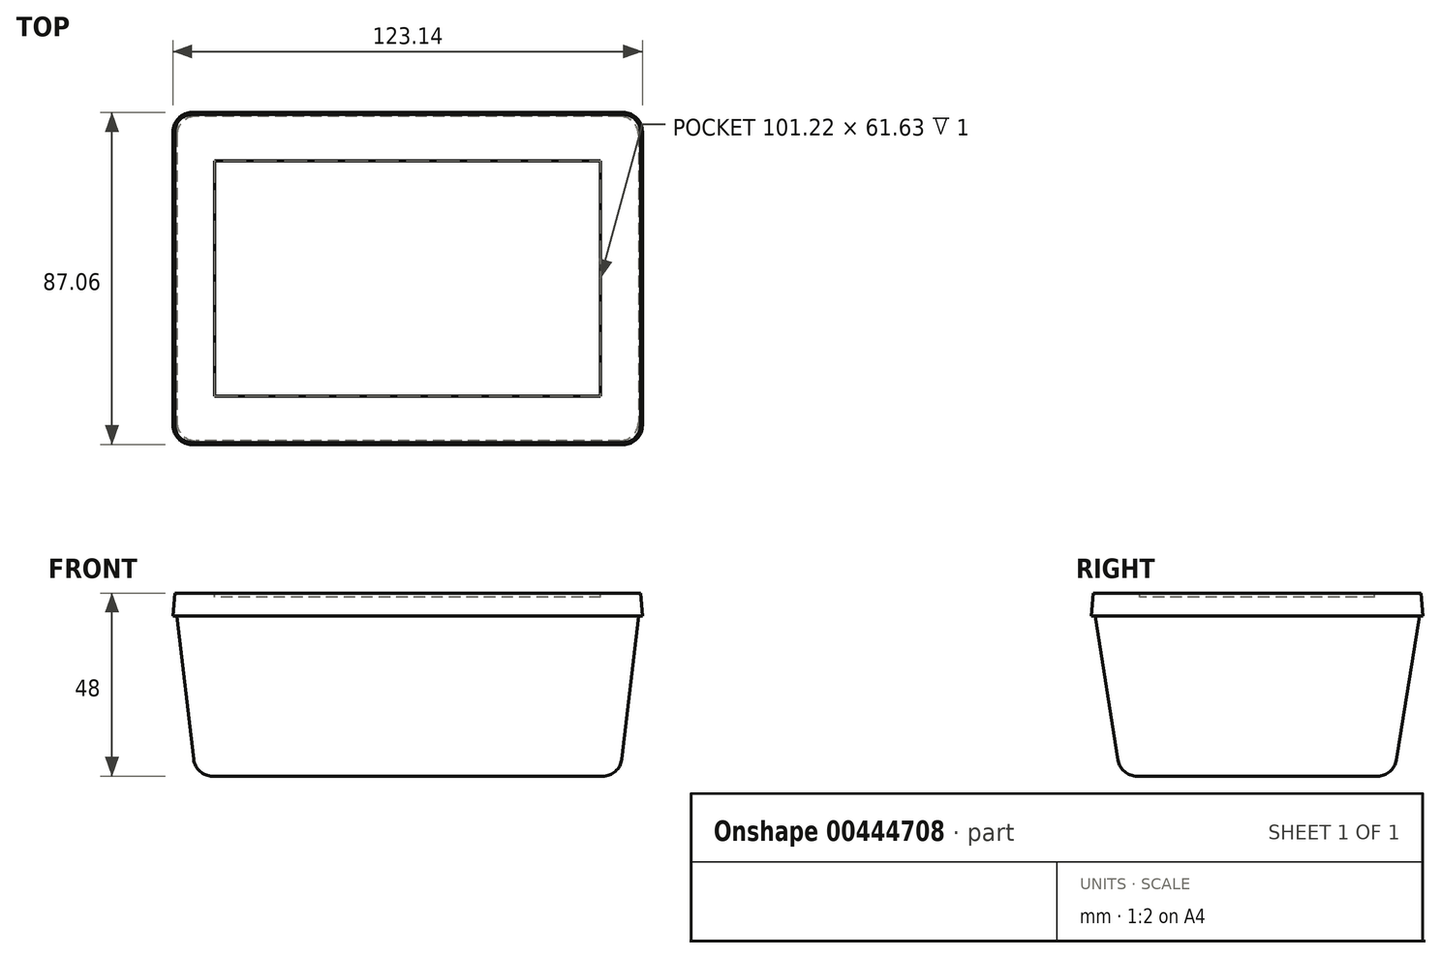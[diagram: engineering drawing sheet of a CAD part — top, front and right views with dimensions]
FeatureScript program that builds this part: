
annotation { "Feature Type Name" : "Feature", "Feature Type Description" : "" }
export const myFeature = defineFeature(function(context is Context, id is Id, definition is map)
    precondition{}
    {
        {
            var Q0;
            Q0=qCreatedBy(makeId("Top.planeOp"),FACE);
            var sketch = newSketch(context, id + "F0", { "sketchPlane" : qUnion([Q0])});
            skLineSegment(sketch, "E0.bottom", {"start": v(55.6, 35.81) * mm, "end": v(-55.6, 35.81) * mm});
            skLineSegment(sketch, "E0.top", {"start": v(55.6, -35.81) * mm, "end": v(-55.6, -35.81) * mm});
            skLineSegment(sketch, "E0.left", {"start": v(55.6, 35.81) * mm, "end": v(55.6, -35.81) * mm});
            skLineSegment(sketch, "E0.right", {"start": v(-55.6, 35.81) * mm, "end": v(-55.6, -35.81) * mm});
            skPoint(sketch, "E0.middle", {"position": v(0, 0) * mm});
            skSolve(sketch);
        }
        {
            var Q0;
            Q0=makeQuery(id+"F0.imprint","IMPRINT",FACE,{"disambiguationData":[TD([[makeQuery(id+"F0.imprint","IMPRINT",EDGE,{"derivedFrom":sQuery(id+"F0.wireOp",EDGE,"E0.bottom")}),1.0]])]});
            cPlane(context, id + "F1", {"entities" : qUnion([Q0]), "cplaneType" : CPlaneType.OFFSET, "offset" : 42 * mm, "width" : 150 * mm, "height" : 150 * mm});
        }
        {
            var Q0;
            Q0=qCreatedBy(id+"F1.planeOp",FACE);
            var sketch = newSketch(context, id + "F2", { "sketchPlane" : qUnion([Q0])});
            skLineSegment(sketch, "E1.bottom", {"start": v(60.57, 42.53) * mm, "end": v(-60.57, 42.53) * mm});
            skLineSegment(sketch, "E1.top", {"start": v(60.57, -42.53) * mm, "end": v(-60.57, -42.53) * mm});
            skLineSegment(sketch, "E1.left", {"start": v(60.57, 42.53) * mm, "end": v(60.57, -42.53) * mm});
            skLineSegment(sketch, "E1.right", {"start": v(-60.57, 42.53) * mm, "end": v(-60.57, -42.53) * mm});
            skPoint(sketch, "E1.middle", {"position": v(0, 0) * mm});
            skSolve(sketch);
        }
        {
            var Q0;
            Q0=makeQuery(id+"F0.imprint","IMPRINT",FACE,{"disambiguationData":[TD([[makeQuery(id+"F0.imprint","IMPRINT",EDGE,{"derivedFrom":sQuery(id+"F0.wireOp",EDGE,"E0.bottom")}),1.0]])]});
            var Q1;
            Q1=makeQuery(id+"F2.imprint","IMPRINT",FACE,{"disambiguationData":[TD([[makeQuery(id+"F2.imprint","IMPRINT",EDGE,{"derivedFrom":sQuery(id+"F2.wireOp",EDGE,"E1.bottom")}),1.0]])]});
            loft(context, id + "F3", {"sheetProfilesArray" : [{ "sheetProfileEntities" : qUnion([Q0]) }, { "sheetProfileEntities" : qUnion([Q1]) }]});
        }
        {
            var Q0;
            Q0=makeQuery(id+"F3.opLoft","MID_CAP_EDGE",EDGE,{"disambiguationData":[OSD([sQuery(id+"F0.wireOp",EDGE,"E0.bottom"),sQuery(id+"F0.wireOp",EDGE,"E0.top"),sQuery(id+"F0.wireOp",EDGE,"E0.right")])],"capPos":0.0});
            var Q1;
            Q1=makeQuery(id+"F3.opLoft","SWEPT_EDGE",EDGE,{"disambiguationData":[OSD([sQuery(id+"F0.wireOp",EDGE,"E0.bottom"),sQuery(id+"F0.wireOp",EDGE,"E0.right"),sQuery(id+"F2.wireOp",EDGE,"E1.bottom"),sQuery(id+"F2.wireOp",EDGE,"E1.right")])]});
            var Q2;
            Q2=makeQuery(id+"F3.opLoft","MID_CAP_EDGE",EDGE,{"disambiguationData":[OSD([sQuery(id+"F0.wireOp",EDGE,"E0.bottom"),sQuery(id+"F0.wireOp",EDGE,"E0.left"),sQuery(id+"F0.wireOp",EDGE,"E0.right")])],"capPos":0.0});
            var Q3;
            Q3=makeQuery(id+"F3.opLoft","MID_CAP_EDGE",EDGE,{"disambiguationData":[OSD([sQuery(id+"F0.wireOp",EDGE,"E0.bottom"),sQuery(id+"F0.wireOp",EDGE,"E0.top"),sQuery(id+"F0.wireOp",EDGE,"E0.left")])],"capPos":0.0});
            var Q4;
            Q4=makeQuery(id+"F3.opLoft","SWEPT_EDGE",EDGE,{"disambiguationData":[OSD([sQuery(id+"F0.wireOp",EDGE,"E0.bottom"),sQuery(id+"F0.wireOp",EDGE,"E0.left"),sQuery(id+"F2.wireOp",EDGE,"E1.bottom"),sQuery(id+"F2.wireOp",EDGE,"E1.left")])]});
            var Q5;
            Q5=makeQuery(id+"F3.opLoft","SWEPT_EDGE",EDGE,{"disambiguationData":[OSD([sQuery(id+"F0.wireOp",EDGE,"E0.top"),sQuery(id+"F0.wireOp",EDGE,"E0.right"),sQuery(id+"F2.wireOp",EDGE,"E1.top"),sQuery(id+"F2.wireOp",EDGE,"E1.right")])]});
            var Q6;
            Q6=makeQuery(id+"F3.opLoft","MID_CAP_EDGE",EDGE,{"disambiguationData":[OSD([sQuery(id+"F0.wireOp",EDGE,"E0.top"),sQuery(id+"F0.wireOp",EDGE,"E0.left"),sQuery(id+"F0.wireOp",EDGE,"E0.right")])],"capPos":0.0});
            var Q7;
            Q7=makeQuery(id+"F3.opLoft","SWEPT_EDGE",EDGE,{"disambiguationData":[OSD([sQuery(id+"F0.wireOp",EDGE,"E0.top"),sQuery(id+"F0.wireOp",EDGE,"E0.left"),sQuery(id+"F2.wireOp",EDGE,"E1.top"),sQuery(id+"F2.wireOp",EDGE,"E1.left")])]});
            fillet(context, id + "F4", {"entities" : qUnion([Q0, Q1, Q2, Q3, Q4, Q5, Q6, Q7]), "radius" : 5 * mm, "tangentPropagation" : true, "allowEdgeOverflow" : false});
        }
        {
            var Q0;
            Q0=makeQuery(id+"F3.opLoft","CAP_FACE",FACE,{"disambiguationData":[OSD([makeQuery(id+"F2.imprint","IMPRINT",FACE,{"disambiguationData":[TD([[makeQuery(id+"F2.imprint","IMPRINT",EDGE,{"derivedFrom":sQuery(id+"F2.wireOp",EDGE,"E1.bottom")}),1.0]])]})])],"isStart":true});
            var sketch = newSketch(context, id + "F5", { "sketchPlane" : qUnion([Q0])});
            skLineSegment(sketch, "E2.bottom", {"start": v(61.57, 43.53) * mm, "end": v(-61.57, 43.53) * mm});
            skLineSegment(sketch, "E2.top", {"start": v(61.57, -43.53) * mm, "end": v(-61.57, -43.53) * mm});
            skLineSegment(sketch, "E2.left", {"start": v(61.57, 43.53) * mm, "end": v(61.57, -43.53) * mm});
            skLineSegment(sketch, "E2.right", {"start": v(-61.57, 43.53) * mm, "end": v(-61.57, -43.53) * mm});
            skPoint(sketch, "E2.middle", {"position": v(0, 0) * mm});
            skSolve(sketch);
        }
        {
            var Q0;
            Q0=makeQuery(id+"F5.imprint","IMPRINT",FACE,{"disambiguationData":[TD([[makeQuery(id+"F5.imprint","IMPRINT",EDGE,{"derivedFrom":sQuery(id+"F5.wireOp",EDGE,"E2.bottom")}),1.0]])]});
            var Q1;
            {var subQ0=sQuery(id+"F2.wireOp",EDGE,"E1.bottom");var subQ2=sQuery(id+"F2.wireOp",EDGE,"E1.left");var subQ3=sQuery(id+"F2.wireOp",EDGE,"E1.right");Q1=makeQuery(id+"F5.imprint","IMPRINT",FACE,{"disambiguationData":[TD([[makeQuery(id+"F5.imprint","IMPRINT",EDGE,{"derivedFrom":makeQuery(id+"F3.opLoft","MID_CAP_EDGE",EDGE,{"disambiguationData":[OSD([subQ0,subQ2,subQ3])],"capPos":1.0})}),1.0]])]});}
            extrude(context, id + "F6", {"entities" : qUnion([Q0, Q1]), "operationType" : NewBodyOperationType.ADD, "depth" : 6 * mm});
        }
        {
            var Q0;
            Q0=makeQuery(id+"F6.opExtrude","CAP_FACE",FACE,{"disambiguationData":[OSD([sQuery(id+"F5.wireOp",EDGE,"E2.bottom"),sQuery(id+"F5.wireOp",EDGE,"E2.top"),sQuery(id+"F5.wireOp",EDGE,"E2.left"),sQuery(id+"F5.wireOp",EDGE,"E2.right")])],"isStart":false});
            var sketch = newSketch(context, id + "F7", { "sketchPlane" : qUnion([Q0])});
            skLineSegment(sketch, "E3.bottom", {"start": v(50.6, 30.82) * mm, "end": v(-50.6, 30.82) * mm});
            skLineSegment(sketch, "E3.top", {"start": v(50.6, -30.82) * mm, "end": v(-50.6, -30.82) * mm});
            skLineSegment(sketch, "E3.left", {"start": v(50.6, 30.82) * mm, "end": v(50.6, -30.82) * mm});
            skLineSegment(sketch, "E3.right", {"start": v(-50.6, 30.82) * mm, "end": v(-50.6, -30.81) * mm});
            skPoint(sketch, "E3.middle", {"position": v(0, 0) * mm});
            skSolve(sketch);
        }
        {
            var Q0;
            Q0 = qSketchRegion(id + "F7", true);
            extrude(context, id + "F8", {"entities" : qUnion([Q0]), "operationType" : NewBodyOperationType.REMOVE, "oppositeDirection" : true, "depth" : 1 * mm});
        }
        {
            var Q0;
            Q0=makeQuery(id+"F6.opExtrude","SWEPT_EDGE",EDGE,{"disambiguationData":[OSD([sQuery(id+"F5.wireOp",EDGE,"E2.bottom"),sQuery(id+"F5.wireOp",EDGE,"E2.right")])]});
            var Q1;
            Q1=makeQuery(id+"F6.opExtrude","SWEPT_EDGE",EDGE,{"disambiguationData":[OSD([sQuery(id+"F5.wireOp",EDGE,"E2.top"),sQuery(id+"F5.wireOp",EDGE,"E2.right")])]});
            var Q2;
            Q2=makeQuery(id+"F6.opExtrude","SWEPT_EDGE",EDGE,{"disambiguationData":[OSD([sQuery(id+"F5.wireOp",EDGE,"E2.top"),sQuery(id+"F5.wireOp",EDGE,"E2.left")])]});
            var Q3;
            Q3=makeQuery(id+"F6.opExtrude","SWEPT_EDGE",EDGE,{"disambiguationData":[OSD([sQuery(id+"F5.wireOp",EDGE,"E2.bottom"),sQuery(id+"F5.wireOp",EDGE,"E2.left")])]});
            fillet(context, id + "F9", {"entities" : qUnion([Q0, Q1, Q2, Q3]), "radius" : 5 * mm, "tangentPropagation" : true, "allowEdgeOverflow" : false});
        }
        {
            var Q0;
            Q0=makeQuery(id+"F6.opExtrude","CAP_EDGE",EDGE,{"disambiguationData":[OSD([sQuery(id+"F5.wireOp",EDGE,"E2.left")])],"isStart":false});
            var Q1;
            {var subQ0=sQuery(id+"F5.wireOp",EDGE,"E2.left");var subQ1=sQuery(id+"F5.wireOp",EDGE,"E2.bottom");Q1=makeQuery(id+"F9.opFillet","BLEND_EDGE",EDGE,{"blendedFrom":[makeQuery(id+"F6.opExtrude","SWEPT_EDGE",EDGE,{"disambiguationData":[OSD([subQ1,subQ0])]}),makeQuery(id+"F6.opExtrude","CAP_FACE",FACE,{"disambiguationData":[OSD([subQ1,sQuery(id+"F5.wireOp",EDGE,"E2.top"),subQ0,sQuery(id+"F5.wireOp",EDGE,"E2.right")])],"isStart":false})],"blendedInto":[makeQuery(id+"F6.opExtrude","CAP_FACE",FACE,{"disambiguationData":[OSD([subQ1,sQuery(id+"F5.wireOp",EDGE,"E2.top"),subQ0,sQuery(id+"F5.wireOp",EDGE,"E2.right")])],"isStart":false})]});}
            var Q2;
            Q2=makeQuery(id+"F6.opExtrude","CAP_EDGE",EDGE,{"disambiguationData":[OSD([sQuery(id+"F5.wireOp",EDGE,"E2.bottom")])],"isStart":false});
            var Q3;
            {var subQ0=sQuery(id+"F5.wireOp",EDGE,"E2.right");var subQ1=sQuery(id+"F5.wireOp",EDGE,"E2.bottom");Q3=makeQuery(id+"F9.opFillet","BLEND_EDGE",EDGE,{"blendedFrom":[makeQuery(id+"F6.opExtrude","SWEPT_EDGE",EDGE,{"disambiguationData":[OSD([subQ1,subQ0])]}),makeQuery(id+"F6.opExtrude","CAP_FACE",FACE,{"disambiguationData":[OSD([subQ1,sQuery(id+"F5.wireOp",EDGE,"E2.top"),sQuery(id+"F5.wireOp",EDGE,"E2.left"),subQ0])],"isStart":false})],"blendedInto":[makeQuery(id+"F6.opExtrude","CAP_FACE",FACE,{"disambiguationData":[OSD([subQ1,sQuery(id+"F5.wireOp",EDGE,"E2.top"),sQuery(id+"F5.wireOp",EDGE,"E2.left"),subQ0])],"isStart":false})]});}
            var Q4;
            Q4=makeQuery(id+"F6.opExtrude","CAP_EDGE",EDGE,{"disambiguationData":[OSD([sQuery(id+"F5.wireOp",EDGE,"E2.right")])],"isStart":false});
            var Q5;
            {var subQ0=sQuery(id+"F5.wireOp",EDGE,"E2.right");var subQ1=sQuery(id+"F5.wireOp",EDGE,"E2.top");Q5=makeQuery(id+"F9.opFillet","BLEND_EDGE",EDGE,{"blendedFrom":[makeQuery(id+"F6.opExtrude","SWEPT_EDGE",EDGE,{"disambiguationData":[OSD([subQ1,subQ0])]}),makeQuery(id+"F6.opExtrude","CAP_FACE",FACE,{"disambiguationData":[OSD([sQuery(id+"F5.wireOp",EDGE,"E2.bottom"),subQ1,sQuery(id+"F5.wireOp",EDGE,"E2.left"),subQ0])],"isStart":false})],"blendedInto":[makeQuery(id+"F6.opExtrude","CAP_FACE",FACE,{"disambiguationData":[OSD([sQuery(id+"F5.wireOp",EDGE,"E2.bottom"),subQ1,sQuery(id+"F5.wireOp",EDGE,"E2.left"),subQ0])],"isStart":false})]});}
            var Q6;
            Q6=makeQuery(id+"F6.opExtrude","CAP_EDGE",EDGE,{"disambiguationData":[OSD([sQuery(id+"F5.wireOp",EDGE,"E2.top")])],"isStart":false});
            var Q7;
            {var subQ0=sQuery(id+"F5.wireOp",EDGE,"E2.left");var subQ1=sQuery(id+"F5.wireOp",EDGE,"E2.top");Q7=makeQuery(id+"F9.opFillet","BLEND_EDGE",EDGE,{"blendedFrom":[makeQuery(id+"F6.opExtrude","SWEPT_EDGE",EDGE,{"disambiguationData":[OSD([subQ1,subQ0])]}),makeQuery(id+"F6.opExtrude","CAP_FACE",FACE,{"disambiguationData":[OSD([sQuery(id+"F5.wireOp",EDGE,"E2.bottom"),subQ1,subQ0,sQuery(id+"F5.wireOp",EDGE,"E2.right")])],"isStart":false})],"blendedInto":[makeQuery(id+"F6.opExtrude","CAP_FACE",FACE,{"disambiguationData":[OSD([sQuery(id+"F5.wireOp",EDGE,"E2.bottom"),subQ1,subQ0,sQuery(id+"F5.wireOp",EDGE,"E2.right")])],"isStart":false})]});}
            chamfer(context, id + "F10", {"entities" : qUnion([Q0, Q1, Q2, Q3, Q4, Q5, Q6, Q7]), "chamferType" : ChamferType.OFFSET_ANGLE, "width" : 6 * mm, "oppositeDirection" : false, "angle" : 5 * degree, "tangentPropagation" : true});
        }
    });
